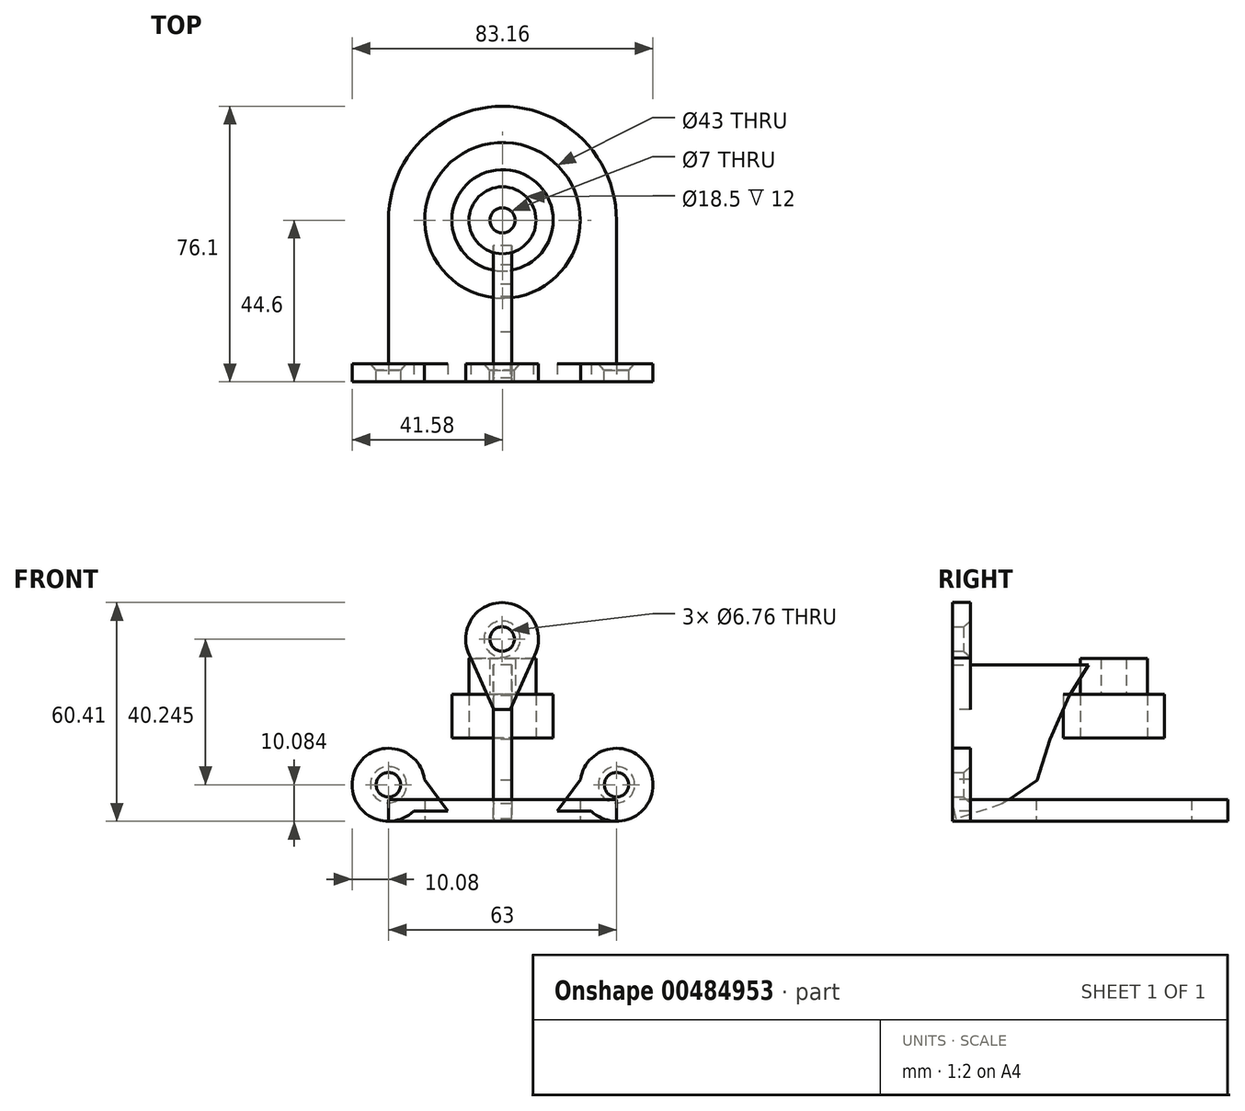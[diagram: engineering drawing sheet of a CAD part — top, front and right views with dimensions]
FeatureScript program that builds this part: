
annotation { "Feature Type Name" : "Feature", "Feature Type Description" : "" }
export const myFeature = defineFeature(function(context is Context, id is Id, definition is map)
    precondition{}
    {
        {
            var Q0;
            Q0=qCreatedBy(makeId("Top.planeOp"),FACE);
            var sketch = newSketch(context, id + "F0", { "sketchPlane" : qUnion([Q0])});
            skCircle(sketch, "E0", {"center": v(0, 0) * mm, "radius": 21.5 * mm});
            skCircle(sketch, "E1.0", {"center": v(0, 0) * mm, "radius": 31.5 * mm});
            skSolve(sketch);
        }
        {
            var Q0;
            Q0=makeQuery(id+"F0.imprint","IMPRINT",FACE,{"disambiguationData":[TD([[makeQuery(id+"F0.imprint","IMPRINT",EDGE,{"derivedFrom":sQuery(id+"F0.wireOp",EDGE,"E0")}),-1.0]])]});
            extrude(context, id + "F1", {"entities" : qUnion([Q0]), "depth" : 6 * mm});
        }
        {
            var Q0;
            Q0=makeQuery(id+"F1.opExtrude","CAP_FACE",FACE,{"disambiguationData":[OSD([sQuery(id+"F0.wireOp",EDGE,"E0"),sQuery(id+"F0.wireOp",EDGE,"E1.0")])],"isStart":false});
            cPlane(context, id + "F2", {"entities" : qUnion([Q0]), "cplaneType" : CPlaneType.OFFSET, "offset" : 6 * mm, "width" : 150 * mm, "height" : 150 * mm});
        }
        {
            var Q0;
            Q0=qCreatedBy(id+"F2.planeOp",FACE);
            var sketch = newSketch(context, id + "F3", { "sketchPlane" : qUnion([Q0])});
            skCircle(sketch, "E2", {"center": v(0, 0) * mm, "radius": 17 * mm});
            skCircle(sketch, "E3.0", {"center": v(0, 0) * mm, "radius": 22 * mm});
            skSolve(sketch);
        }
        {
            var Q0;
            Q0=qCreatedBy(id+"F2.planeOp",FACE);
            cPlane(context, id + "F4", {"entities" : qUnion([Q0]), "cplaneType" : CPlaneType.OFFSET, "offset" : 11 * mm, "width" : 150 * mm, "height" : 150 * mm});
        }
        {
            var Q0;
            Q0=qCreatedBy(id+"F4.planeOp",FACE);
            var sketch = newSketch(context, id + "F5", { "sketchPlane" : qUnion([Q0])});
            skCircle(sketch, "E4", {"center": v(0, 0) * mm, "radius": 9.25 * mm});
            skCircle(sketch, "E5", {"center": v(0, 0) * mm, "radius": 14 * mm});
            skCircle(sketch, "E6.0", {"center": v(0, 0) * mm, "radius": 19 * mm});
            skSolve(sketch);
        }
        {
            var Q0;
            Q0=qCreatedBy(id+"F4.planeOp",FACE);
            cPlane(context, id + "F6", {"entities" : qUnion([Q0]), "cplaneType" : CPlaneType.OFFSET, "offset" : 12 * mm, "width" : 150 * mm, "height" : 150 * mm});
        }
        {
            var Q0;
            Q0=qCreatedBy(id+"F6.planeOp",FACE);
            var sketch = newSketch(context, id + "F7", { "sketchPlane" : qUnion([Q0])});
            skCircle(sketch, "E7", {"center": v(0, 0) * mm, "radius": 3.5 * mm});
            skCircle(sketch, "E8", {"center": v(0, 0) * mm, "radius": 9.25 * mm});
            skCircle(sketch, "E9.0", {"center": v(0, 0) * mm, "radius": 14.25 * mm});
            skSolve(sketch);
        }
        {
            var Q0;
            Q0=sQuery(id+"F3.wireOp",EDGE,"E2");
            var Q1;
            Q1=makeQuery(id+"F1.opExtrude","CAP_EDGE",EDGE,{"disambiguationData":[OSD([sQuery(id+"F0.wireOp",EDGE,"E0")])],"isStart":false});
            loft(context, id + "F8", {"bodyType" : ToolBodyType.SURFACE, "wireProfilesArray" : [{ "wireProfileEntities" : qUnion([Q0]) }, { "wireProfileEntities" : qUnion([Q1]) }]});
        }
        {
            var Q0;
            Q0=sQuery(id+"F3.wireOp",EDGE,"E3.0");
            var Q1;
            Q1=makeQuery(id+"F1.opExtrude","CAP_EDGE",EDGE,{"disambiguationData":[OSD([sQuery(id+"F0.wireOp",EDGE,"E1.0")])],"isStart":false});
            loft(context, id + "F9", {"bodyType" : ToolBodyType.SURFACE, "wireProfilesArray" : [{ "wireProfileEntities" : qUnion([Q0]) }, { "wireProfileEntities" : qUnion([Q1]) }]});
        }
        {
            var Q0;
            Q0=sQuery(id+"F5.wireOp",EDGE,"E5");
            var Q1;
            Q1=sQuery(id+"F3.wireOp",EDGE,"E2");
            loft(context, id + "F10", {"bodyType" : ToolBodyType.SURFACE, "wireProfilesArray" : [{ "wireProfileEntities" : qUnion([Q0]) }, { "wireProfileEntities" : qUnion([Q1]) }]});
        }
        {
            var Q0;
            Q0=sQuery(id+"F5.wireOp",EDGE,"E6.0");
            var Q1;
            Q1=sQuery(id+"F3.wireOp",EDGE,"E3.0");
            loft(context, id + "F11", {"bodyType" : ToolBodyType.SURFACE, "wireProfilesArray" : [{ "wireProfileEntities" : qUnion([Q0]) }, { "wireProfileEntities" : qUnion([Q1]) }]});
        }
        {
            var Q0;
            Q0=makeQuery(id+"F5.imprint","IMPRINT",FACE,{"disambiguationData":[TD([[makeQuery(id+"F5.imprint","IMPRINT",EDGE,{"derivedFrom":sQuery(id+"F5.wireOp",EDGE,"E4")}),-1.0]])]});
            extrude(context, id + "F12", {"entities" : qUnion([Q0]), "depth" : 12 * mm});
        }
        {
            var Q0;
            Q0=makeQuery(id+"F7.imprint","IMPRINT",FACE,{"disambiguationData":[TD([[makeQuery(id+"F7.imprint","IMPRINT",EDGE,{"derivedFrom":sQuery(id+"F7.wireOp",EDGE,"E7")}),-1.0]])]});
            extrude(context, id + "F13", {"entities" : qUnion([Q0]), "depth" : 10 * mm});
        }
        {
            var Q0;
            Q0=sQuery(id+"F7.wireOp",EDGE,"E9.0");
            var Q1;
            Q1=sQuery(id+"F5.wireOp",EDGE,"E6.0");
            loft(context, id + "F14", {"bodyType" : ToolBodyType.SURFACE, "wireProfilesArray" : [{ "wireProfileEntities" : qUnion([Q0]) }, { "wireProfileEntities" : qUnion([Q1]) }]});
        }
        {
            var Q0;
            Q0=makeQuery(id+"F13.opExtrude","CAP_FACE",FACE,{"disambiguationData":[OSD([sQuery(id+"F7.wireOp",EDGE,"E7"),sQuery(id+"F7.wireOp",EDGE,"E8")])],"isStart":false});
            var Q1;
            Q1=makeQuery(id+"F13.opExtrude","CAP_EDGE",EDGE,{"disambiguationData":[OSD([sQuery(id+"F7.wireOp",EDGE,"E8")])],"isStart":false});
            var Q2;
            Q2=sQuery(id+"F7.wireOp",EDGE,"E9.0");
            loft(context, id + "F15", {"bodyType" : ToolBodyType.SURFACE, "sheetProfilesArray" : [{ "sheetProfileEntities" : qUnion([Q0]) }], "wireProfilesArray" : [{ "wireProfileEntities" : qUnion([Q1]) }, { "wireProfileEntities" : qUnion([Q2]) }]});
        }
        {
            var Q0;
            Q0=makeQuery(id+"F1.opExtrude","CAP_FACE",FACE,{"disambiguationData":[OSD([sQuery(id+"F0.wireOp",EDGE,"E0"),sQuery(id+"F0.wireOp",EDGE,"E1.0")])],"isStart":true});
            var sketch = newSketch(context, id + "F16", { "sketchPlane" : qUnion([Q0])});
            skLineSegment(sketch, "E10.top", {"start": v(31.5, 44.6) * mm, "end": v(-31.5, 44.6) * mm});
            skLineSegment(sketch, "E10.left", {"start": v(31.5, -0.05) * mm, "end": v(31.5, 44.6) * mm});
            skLineSegment(sketch, "E10.right", {"start": v(-31.5, -0.05) * mm, "end": v(-31.5, 44.6) * mm});
            skArc(sketch, "E11", {"start": v(31.5, -0.05) * mm, "mid": v(0, 24.86) * mm, "end": v(-31.5, -0.05) * mm});
            skSolve(sketch);
        }
        {
            var Q0;
            {var subQ0=sQuery(id+"F16.wireOp",EDGE,"E10.top");Q0=makeQuery(id+"F16.imprint","IMPRINT",FACE,{"disambiguationData":[TD([[makeQuery(id+"F16.imprint","IMPRINT",EDGE,{"derivedFrom":subQ0}),1.0]])]});}
            extrude(context, id + "F17", {"entities" : qUnion([Q0]), "operationType" : NewBodyOperationType.ADD, "oppositeDirection" : true, "depth" : 6 * mm});
        }
        {
            var Q0;
            Q0=qCreatedBy(makeId("Right.planeOp"),FACE);
            var sketch = newSketch(context, id + "F18", { "sketchPlane" : qUnion([Q0])});
            skLineSegment(sketch, "E12", {"start": v(-7, 43.22) * mm, "end": v(-12.3, 34.64) * mm});
            skLineSegment(sketch, "E13", {"start": v(-12.3, 34.64) * mm, "end": v(-17.66, 22.62) * mm});
            skLineSegment(sketch, "E14", {"start": v(-17.66, 22.62) * mm, "end": v(-21.13, 11.3) * mm});
            skLineSegment(sketch, "E15", {"start": v(-21.13, 11.3) * mm, "end": v(-30.84, 4.74) * mm});
            skLineSegment(sketch, "E16", {"start": v(-30.84, 4.74) * mm, "end": v(-43.6, 0.65) * mm});
            skLineSegment(sketch, "E17", {"start": v(-43.6, 0.65) * mm, "end": v(-44.54, 5.94) * mm});
            skLineSegment(sketch, "E18", {"start": v(-44.54, 5.94) * mm, "end": v(-44.54, 43.22) * mm});
            skLineSegment(sketch, "E19", {"start": v(-44.54, 43.22) * mm, "end": v(-7, 43.22) * mm});
            skSolve(sketch);
        }
        {
            var Q0;
            Q0 = qSketchRegion(id + "F18", true);
            extrude(context, id + "F19", {"entities" : qUnion([Q0]), "endBound" : BoundingType.SYMMETRIC, "depth" : 5 * mm});
        }
        {
            var Q0;
            Q0=makeQuery(id+"F17.opExtrude","SWEPT_FACE",FACE,{"disambiguationData":[OSD([sQuery(id+"F16.wireOp",EDGE,"E10.top")])]});
            var sketch = newSketch(context, id + "F20", { "sketchPlane" : qUnion([Q0])});
            skPoint(sketch, "E20.first.point", {"position": v(0, 6) * mm});
            skPoint(sketch, "E20.second.point", {"position": v(0, -15.93) * mm});
            skPoint(sketch, "E20.second.point.positionSnap0", {"position": v(0, 6) * mm});
            skPoint(sketch, "E20.third.point", {"position": v(-2.83, -15.54) * mm});
            skPoint(sketch, "E21", {"position": v(0.1, -4.97) * mm});
            skCircle(sketch, "E22", {"center": v(-0.11, 50.29) * mm, "radius": 10.08 * mm});
            skLineSegment(sketch, "E23", {"start": v(8.49, 45.03) * mm, "end": v(2.16, 30.84) * mm});
            skLineSegment(sketch, "E24", {"start": v(2.16, 30.84) * mm, "end": v(-2.41, 30.84) * mm});
            skLineSegment(sketch, "E25", {"start": v(-2.41, 30.84) * mm, "end": v(-8.71, 45.03) * mm});
            skCircle(sketch, "E26", {"center": v(-31.5, 10.04) * mm, "radius": 10.08 * mm});
            skLineSegment(sketch, "E27", {"start": v(-21.54, 11.57) * mm, "end": v(-15.07, 2.73) * mm});
            skLineSegment(sketch, "E28", {"start": v(-15.07, 2.73) * mm, "end": v(-24.56, 2.73) * mm});
            skCircle(sketch, "E29.MirrorC", {"center": v(31.5, 10.04) * mm, "radius": 10.08 * mm});
            skLineSegment(sketch, "E30.MirrorCS", {"start": v(21.54, 11.57) * mm, "end": v(15.07, 2.73) * mm});
            skLineSegment(sketch, "E31.MirrorCS", {"start": v(15.07, 2.73) * mm, "end": v(24.56, 2.73) * mm});
            skSolve(sketch);
        }
        {
            var Q0;
            Q0 = qSketchRegion(id + "F20", true);
            extrude(context, id + "F21", {"entities" : qUnion([Q0]), "oppositeDirection" : true, "depth" : 5 * mm});
        }
        {
            var Q0;
            Q0=makeQuery(id+"F21.opExtrude","CAP_FACE",FACE,{"disambiguationData":[OSD([sQuery(id+"F20.wireOp",EDGE,"E22"),sQuery(id+"F20.wireOp",EDGE,"E23"),sQuery(id+"F20.wireOp",EDGE,"E24"),sQuery(id+"F20.wireOp",EDGE,"E25")])],"isStart":false});
            var sketch = newSketch(context, id + "F22", { "sketchPlane" : qUnion([Q0])});
            skPoint(sketch, "E32", {"position": v(0.11, 50.29) * mm});
            skSolve(sketch);
        }
        {
            var Q0;
            Q0=sQuery(id+"F22.wireOp",VERTEX,"E32");
            var Q1;
            Q1=makeQuery(id+"F21.opExtrude","SWEPT_BODY",BODY,{"disambiguationData":[OSD([sQuery(id+"F20.wireOp",EDGE,"E22"),sQuery(id+"F20.wireOp",EDGE,"E23"),sQuery(id+"F20.wireOp",EDGE,"E24"),sQuery(id+"F20.wireOp",EDGE,"E25")])]});
            hole(context, id + "F23", {"style" : HoleStyle.C_SINK, "endStyle" : HoleEndStyle.THROUGH, "holeDiameter" : 6.76 * mm, "cSinkDiameter" : 10 * mm, "cSinkAngle" : 82 * degree, "isTappedThrough" : true, "tappedDepth" : 12 * mm, "tapClearance" : 3, "locations" : qUnion([Q0]), "scope" : qUnion([Q1])});
        }
        {
            var Q0;
            Q0=makeQuery(id+"F21.opExtrude","CAP_FACE",FACE,{"disambiguationData":[OSD([sQuery(id+"F20.wireOp",EDGE,"E29.MirrorC"),sQuery(id+"F20.wireOp",EDGE,"E30.MirrorCS"),sQuery(id+"F20.wireOp",EDGE,"E31.MirrorCS")])],"isStart":false});
            var sketch = newSketch(context, id + "F24", { "sketchPlane" : qUnion([Q0])});
            skPoint(sketch, "E33", {"position": v(-31.5, 10.04) * mm});
            skSolve(sketch);
        }
        {
            var Q0;
            Q0=makeQuery(id+"F21.opExtrude","CAP_FACE",FACE,{"disambiguationData":[OSD([sQuery(id+"F20.wireOp",EDGE,"E26"),sQuery(id+"F20.wireOp",EDGE,"E27"),sQuery(id+"F20.wireOp",EDGE,"E28")])],"isStart":false});
            var sketch = newSketch(context, id + "F25", { "sketchPlane" : qUnion([Q0])});
            skPoint(sketch, "E34", {"position": v(31.5, 10.04) * mm});
            skSolve(sketch);
        }
        {
            var Q0;
            Q0=sQuery(id+"F24.wireOp",VERTEX,"E33");
            var Q1;
            Q1=sQuery(id+"F25.wireOp",VERTEX,"E34");
            var Q2;
            Q2=makeQuery(id+"F21.opExtrude","SWEPT_BODY",BODY,{"disambiguationData":[OSD([sQuery(id+"F20.wireOp",EDGE,"E26"),sQuery(id+"F20.wireOp",EDGE,"E27"),sQuery(id+"F20.wireOp",EDGE,"E28")])]});
            var Q3;
            Q3=makeQuery(id+"F21.opExtrude","SWEPT_BODY",BODY,{"disambiguationData":[OSD([sQuery(id+"F20.wireOp",EDGE,"E29.MirrorC"),sQuery(id+"F20.wireOp",EDGE,"E30.MirrorCS"),sQuery(id+"F20.wireOp",EDGE,"E31.MirrorCS")])]});
            hole(context, id + "F26", {"style" : HoleStyle.C_SINK, "endStyle" : HoleEndStyle.THROUGH, "holeDiameter" : 6.76 * mm, "cSinkDiameter" : 10 * mm, "cSinkAngle" : 82 * degree, "isTappedThrough" : true, "tappedDepth" : 12 * mm, "tapClearance" : 3, "locations" : qUnion([Q0, Q1]), "scope" : qUnion([Q2, Q3])});
        }
    });
